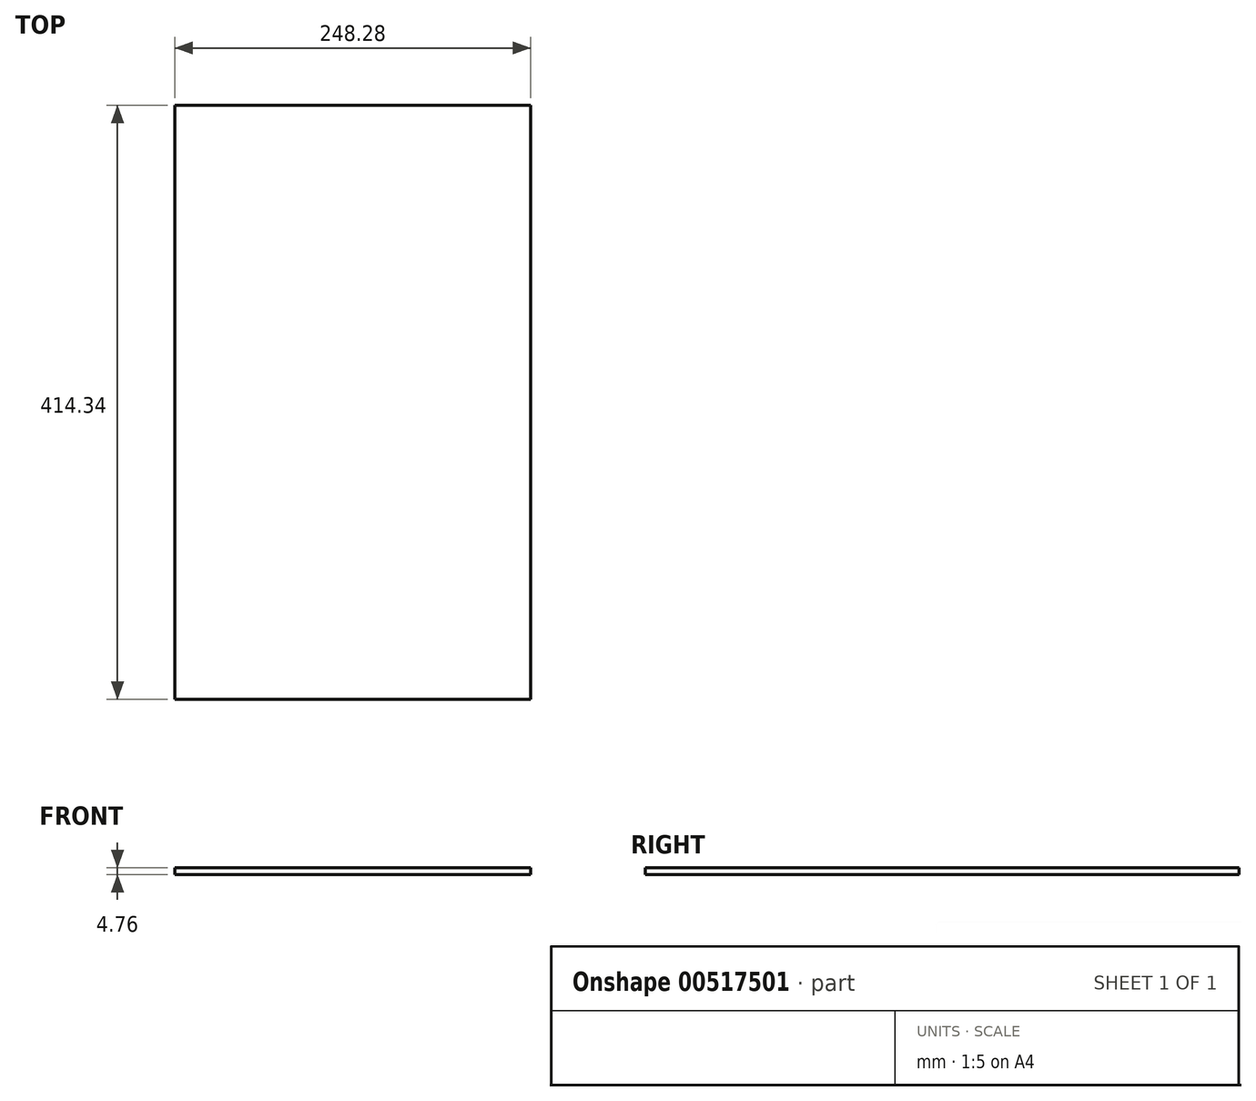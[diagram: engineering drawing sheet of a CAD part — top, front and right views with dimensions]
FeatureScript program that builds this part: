
annotation { "Feature Type Name" : "Feature", "Feature Type Description" : "" }
export const myFeature = defineFeature(function(context is Context, id is Id, definition is map)
    precondition{}
    {
        {
            var Q0;
            Q0=qCreatedBy(makeId("Top.planeOp"),FACE);
            var sketch = newSketch(context, id + "F0", { "sketchPlane" : qUnion([Q0])});
            skLineSegment(sketch, "E0.bottom", {"start": v(-124.14, 207.17) * mm, "end": v(124.14, 207.17) * mm});
            skLineSegment(sketch, "E0.top", {"start": v(-124.14, -207.17) * mm, "end": v(124.14, -207.17) * mm});
            skLineSegment(sketch, "E0.left", {"start": v(-124.14, 207.17) * mm, "end": v(-124.14, -207.17) * mm});
            skLineSegment(sketch, "E0.right", {"start": v(124.14, 207.17) * mm, "end": v(124.14, -207.17) * mm});
            skPoint(sketch, "E0.middle", {"position": v(0, 0) * mm});
            skSolve(sketch);
        }
        {
            var Q0;
            Q0 = qSketchRegion(id + "F0", true);
            extrude(context, id + "F1", {"entities" : qUnion([Q0]), "depth" : 4.76 * mm, "offsetDistance" : 25.4 * mm});
        }
    });
